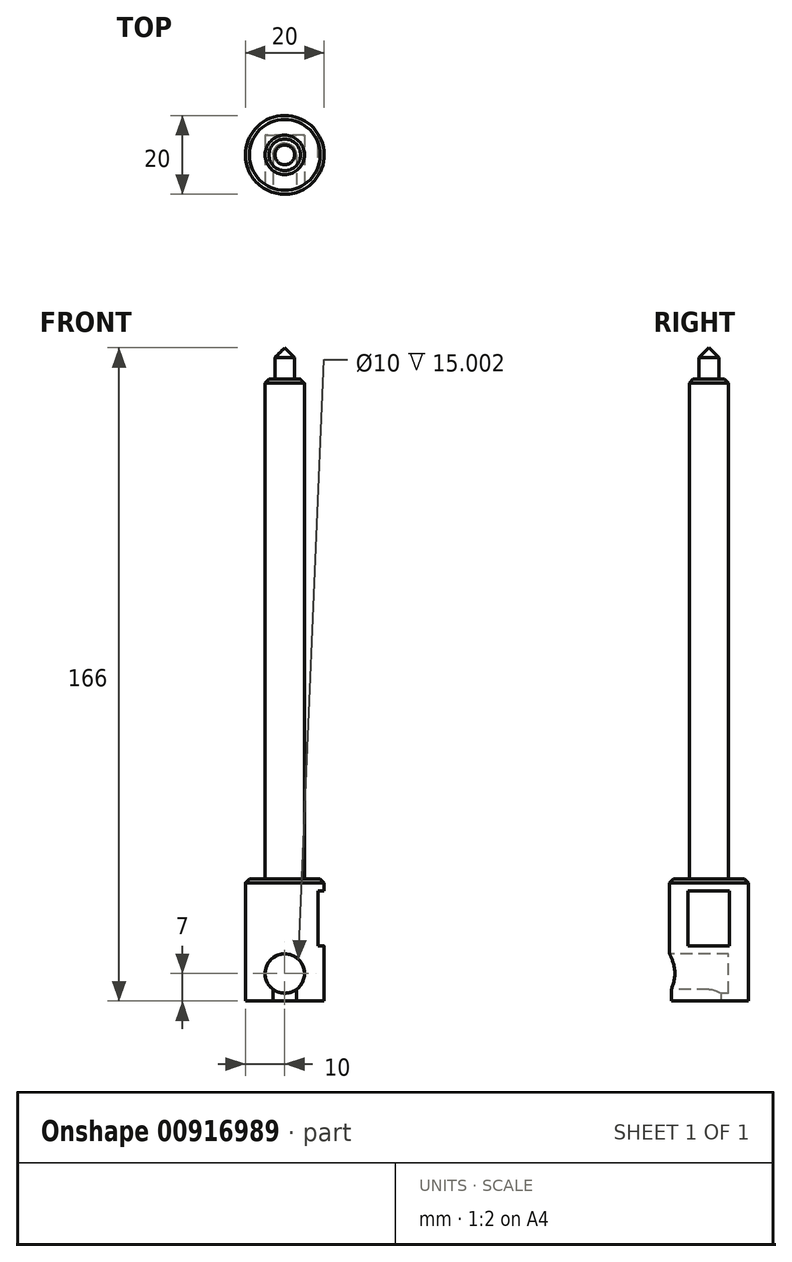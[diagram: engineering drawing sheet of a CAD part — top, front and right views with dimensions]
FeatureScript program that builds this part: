
annotation { "Feature Type Name" : "Feature", "Feature Type Description" : "" }
export const myFeature = defineFeature(function(context is Context, id is Id, definition is map)
    precondition{}
    {
        {
            var Q0;
            Q0=qCreatedBy(makeId("Top.planeOp"),FACE);
            var sketch = newSketch(context, id + "F0", { "sketchPlane" : qUnion([Q0])});
            skCircle(sketch, "E0", {"center": v(0, 0) * mm, "radius": 5 * mm});
            skSolve(sketch);
        }
        {
            var Q0;
            Q0=makeQuery(id+"F0.imprint","IMPRINT",FACE,{"disambiguationData":[TD([[makeQuery(id+"F0.imprint","IMPRINT",EDGE,{"derivedFrom":sQuery(id+"F0.wireOp",EDGE,"E0")}),1.0]])]});
            extrude(context, id + "F1", {"entities" : qUnion([Q0]), "depth" : 127 * mm, "offsetDistance" : 25 * mm});
        }
        {
            var Q0;
            Q0=makeQuery(id+"F1.opExtrude","CAP_FACE",FACE,{"disambiguationData":[OSD([sQuery(id+"F0.wireOp",EDGE,"E0")])],"isStart":false});
            var sketch = newSketch(context, id + "F2", { "sketchPlane" : qUnion([Q0])});
            skCircle(sketch, "E1", {"center": v(0, 0) * mm, "radius": 2.5 * mm});
            skSolve(sketch);
        }
        {
            var Q0;
            Q0=makeQuery(id+"F2.imprint","IMPRINT",FACE,{"disambiguationData":[TD([[makeQuery(id+"F2.imprint","IMPRINT",EDGE,{"derivedFrom":sQuery(id+"F2.wireOp",EDGE,"E1")}),1.0]])]});
            extrude(context, id + "F3", {"entities" : qUnion([Q0]), "operationType" : NewBodyOperationType.ADD, "depth" : 8 * mm, "offsetDistance" : 25 * mm});
        }
        {
            var Q0;
            Q0=makeQuery(id+"F3.opExtrude","CAP_EDGE",EDGE,{"disambiguationData":[OSD([sQuery(id+"F2.wireOp",EDGE,"E1")])],"isStart":false});
            chamfer(context, id + "F4", {"entities" : qUnion([Q0]), "width" : 2.5 * mm, "tangentPropagation" : true});
        }
        {
            var Q0;
            Q0=makeQuery(id+"F1.opExtrude","CAP_EDGE",EDGE,{"disambiguationData":[OSD([sQuery(id+"F0.wireOp",EDGE,"E0")])],"isStart":false});
            chamfer(context, id + "F5", {"entities" : qUnion([Q0]), "width" : 1 * mm, "tangentPropagation" : true});
        }
        {
            var Q0;
            Q0=makeQuery(id+"F1.opExtrude","CAP_FACE",FACE,{"disambiguationData":[OSD([sQuery(id+"F0.wireOp",EDGE,"E0")])],"isStart":true});
            var sketch = newSketch(context, id + "F6", { "sketchPlane" : qUnion([Q0])});
            skCircle(sketch, "E2", {"center": v(0, 0) * mm, "radius": 10 * mm});
            skSolve(sketch);
        }
        {
            var Q0;
            Q0=makeQuery(id+"F6.imprint","IMPRINT",FACE,{"disambiguationData":[TD([[makeQuery(id+"F6.imprint","IMPRINT",EDGE,{"derivedFrom":sQuery(id+"F6.wireOp",EDGE,"E2")}),1.0]])]});
            var Q1;
            Q1=makeQuery(id+"F6.imprint","IMPRINT",FACE,{"disambiguationData":[TD([[makeQuery(id+"F6.imprint","IMPRINT",EDGE,{"derivedFrom":makeQuery(id+"F1.opExtrude","CAP_EDGE",EDGE,{"disambiguationData":[OSD([sQuery(id+"F0.wireOp",EDGE,"E0")])],"isStart":true})}),-1.0]])]});
            extrude(context, id + "F7", {"entities" : qUnion([Q0, Q1]), "operationType" : NewBodyOperationType.ADD, "depth" : 31 * mm, "offsetDistance" : 25 * mm});
        }
        {
            var Q0;
            Q0=qCreatedBy(makeId("Front.planeOp"),FACE);
            cPlane(context, id + "F8", {"entities" : qUnion([Q0]), "cplaneType" : CPlaneType.OFFSET, "offset" : 10 * mm, "width" : 150 * mm, "height" : 150 * mm});
        }
        {
            var Q0;
            Q0=qCreatedBy(id+"F8.planeOp",FACE);
            var sketch = newSketch(context, id + "F9", { "sketchPlane" : qUnion([Q0])});
            skCircle(sketch, "E3", {"center": v(0, -24) * mm, "radius": 5 * mm});
            skSolve(sketch);
        }
        {
            var Q0;
            Q0=makeQuery(id+"F9.imprint","IMPRINT",FACE,{"disambiguationData":[TD([[makeQuery(id+"F9.imprint","IMPRINT",EDGE,{"derivedFrom":sQuery(id+"F9.wireOp",EDGE,"E3")}),1.0]])]});
            extrude(context, id + "F10", {"entities" : qUnion([Q0]), "operationType" : NewBodyOperationType.REMOVE, "oppositeDirection" : true, "depth" : 15 * mm, "offsetDistance" : 25 * mm});
        }
        {
            var Q0;
            Q0=makeQuery(id+"F7.opExtrude","CAP_FACE",FACE,{"disambiguationData":[OSD([sQuery(id+"F6.wireOp",EDGE,"E2")])],"isStart":false});
            var sketch = newSketch(context, id + "F11", { "sketchPlane" : qUnion([Q0])});
            skArc(sketch, "E4", {"start": v(-3, 0) * mm, "mid": v(0, -3) * mm, "end": v(3, 0) * mm});
            skArc(sketch, "E5", {"start": v(3, 9.54) * mm, "mid": v(0, 10) * mm, "end": v(-3, 9.54) * mm});
            skLineSegment(sketch, "E6", {"start": v(-3, 0) * mm, "end": v(-3, 9.54) * mm});
            skLineSegment(sketch, "E7", {"start": v(3, 0) * mm, "end": v(3, 9.54) * mm});
            skSolve(sketch);
        }
        {
            var Q0;
            Q0=makeQuery(id+"F11.imprint","IMPRINT",FACE,{"disambiguationData":[TD([[makeQuery(id+"F11.imprint","IMPRINT",EDGE,{"derivedFrom":sQuery(id+"F11.wireOp",EDGE,"E4")}),1.0]])]});
            extrude(context, id + "F12", {"entities" : qUnion([Q0]), "operationType" : NewBodyOperationType.REMOVE, "oppositeDirection" : true, "depth" : 8 * mm, "offsetDistance" : 25 * mm});
        }
        {
            var Q0;
            Q0=makeQuery(id+"F7.opExtrude","CAP_EDGE",EDGE,{"disambiguationData":[OSD([sQuery(id+"F6.wireOp",EDGE,"E2")])],"isStart":true});
            chamfer(context, id + "F13", {"entities" : qUnion([Q0]), "width" : 1 * mm, "tangentPropagation" : true});
        }
        {
            var Q0;
            Q0=qCreatedBy(makeId("Right.planeOp"),FACE);
            cPlane(context, id + "F14", {"entities" : qUnion([Q0]), "cplaneType" : CPlaneType.OFFSET, "offset" : 10 * mm, "width" : 150 * mm, "height" : 150 * mm});
        }
        {
            var Q0;
            Q0=qCreatedBy(id+"F14.planeOp",FACE);
            var sketch = newSketch(context, id + "F15", { "sketchPlane" : qUnion([Q0])});
            skLineSegment(sketch, "E8.bottom", {"start": v(-5.75, -3) * mm, "end": v(5.75, -3) * mm});
            skLineSegment(sketch, "E8.top", {"start": v(-5.75, -17) * mm, "end": v(5.75, -17) * mm});
            skLineSegment(sketch, "E8.left", {"start": v(-5.75, -3) * mm, "end": v(-5.75, -17) * mm});
            skLineSegment(sketch, "E8.right", {"start": v(5.75, -3) * mm, "end": v(5.75, -17) * mm});
            skSolve(sketch);
        }
        {
            var Q0;
            Q0=makeQuery(id+"F15.imprint","IMPRINT",FACE,{"disambiguationData":[TD([[makeQuery(id+"F15.imprint","IMPRINT",EDGE,{"derivedFrom":sQuery(id+"F15.wireOp",EDGE,"E8.bottom")}),-1.0]])]});
            extrude(context, id + "F16", {"entities" : qUnion([Q0]), "operationType" : NewBodyOperationType.REMOVE, "oppositeDirection" : true, "depth" : 1.5 * mm, "offsetDistance" : 25 * mm});
        }
    });
